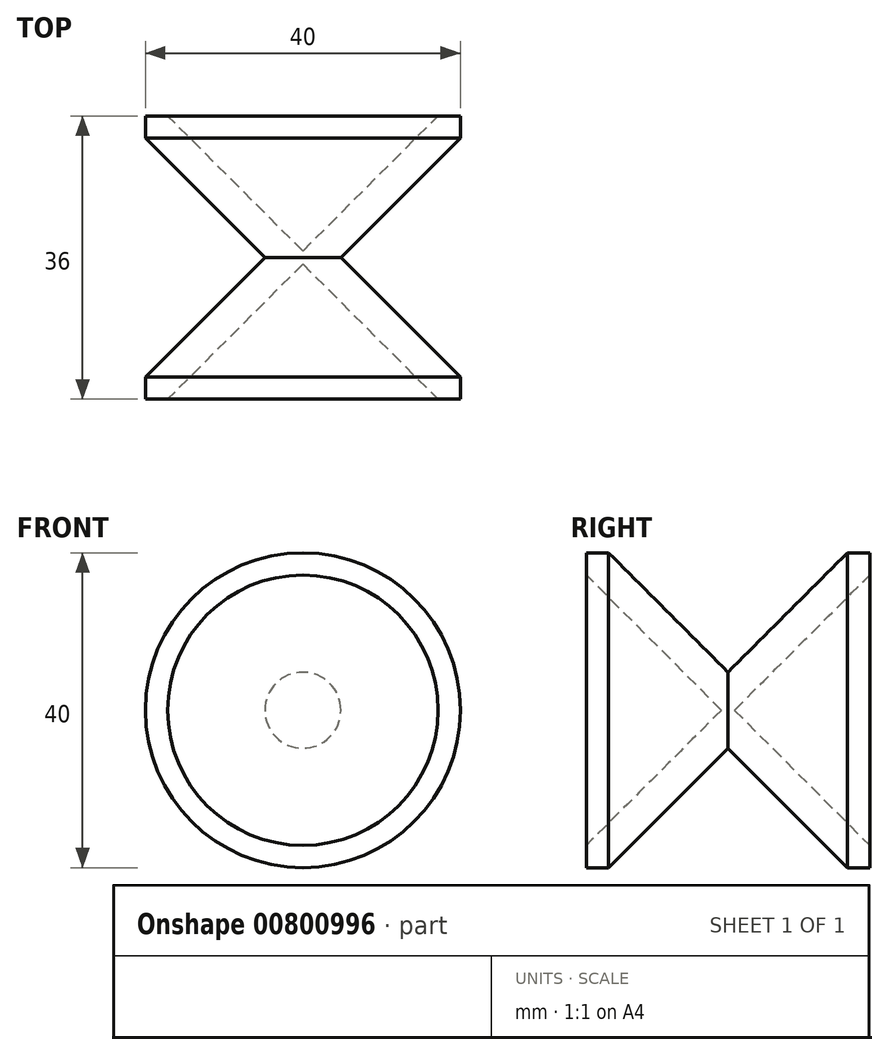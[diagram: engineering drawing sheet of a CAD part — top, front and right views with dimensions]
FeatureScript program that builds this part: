
annotation { "Feature Type Name" : "Feature", "Feature Type Description" : "" }
export const myFeature = defineFeature(function(context is Context, id is Id, definition is map)
    precondition{}
    {
        {
            var Q0;
            Q0=qCreatedBy(makeId("Top.planeOp"),FACE);
            var sketch = newSketch(context, id + "F0", { "sketchPlane" : qUnion([Q0])});
            skLineSegment(sketch, "E0", {"start": v(17.17, 0) * mm, "end": v(0, -17.17) * mm});
            skLineSegment(sketch, "E1", {"start": v(0, -17.17) * mm, "end": v(0, -18.83) * mm});
            skLineSegment(sketch, "E2", {"start": v(0, -18.83) * mm, "end": v(17.17, -36) * mm});
            skLineSegment(sketch, "E3", {"start": v(17.17, -36) * mm, "end": v(20, -36) * mm});
            skLineSegment(sketch, "E4", {"start": v(20, -36) * mm, "end": v(20, -33.17) * mm});
            skLineSegment(sketch, "E5", {"start": v(20, -33.17) * mm, "end": v(4.83, -18) * mm});
            skLineSegment(sketch, "E6", {"start": v(4.83, -18) * mm, "end": v(20, -2.83) * mm});
            skLineSegment(sketch, "E7", {"start": v(20, -2.83) * mm, "end": v(20, 0) * mm});
            skLineSegment(sketch, "E8", {"start": v(20, 0) * mm, "end": v(17.17, 0) * mm});
            skSolve(sketch);
        }
        {
            var Q0;
            Q0=makeQuery(id+"F0.imprint","IMPRINT",FACE,{"disambiguationData":[TD([[makeQuery(id+"F0.imprint","IMPRINT",EDGE,{"derivedFrom":sQuery(id+"F0.wireOp",EDGE,"E0")}),1.0]])]});
            var Q1;
            Q1=sQuery(id+"F0.wireOp",EDGE,"E1");
            revolve(context, id + "F1", {"surfaceOperationType" : NewSurfaceOperationType.NEW, "entities" : qUnion([Q0]), "axis" : qUnion([Q1]), "revolveType" : RevolveType.FULL});
        }
    });
